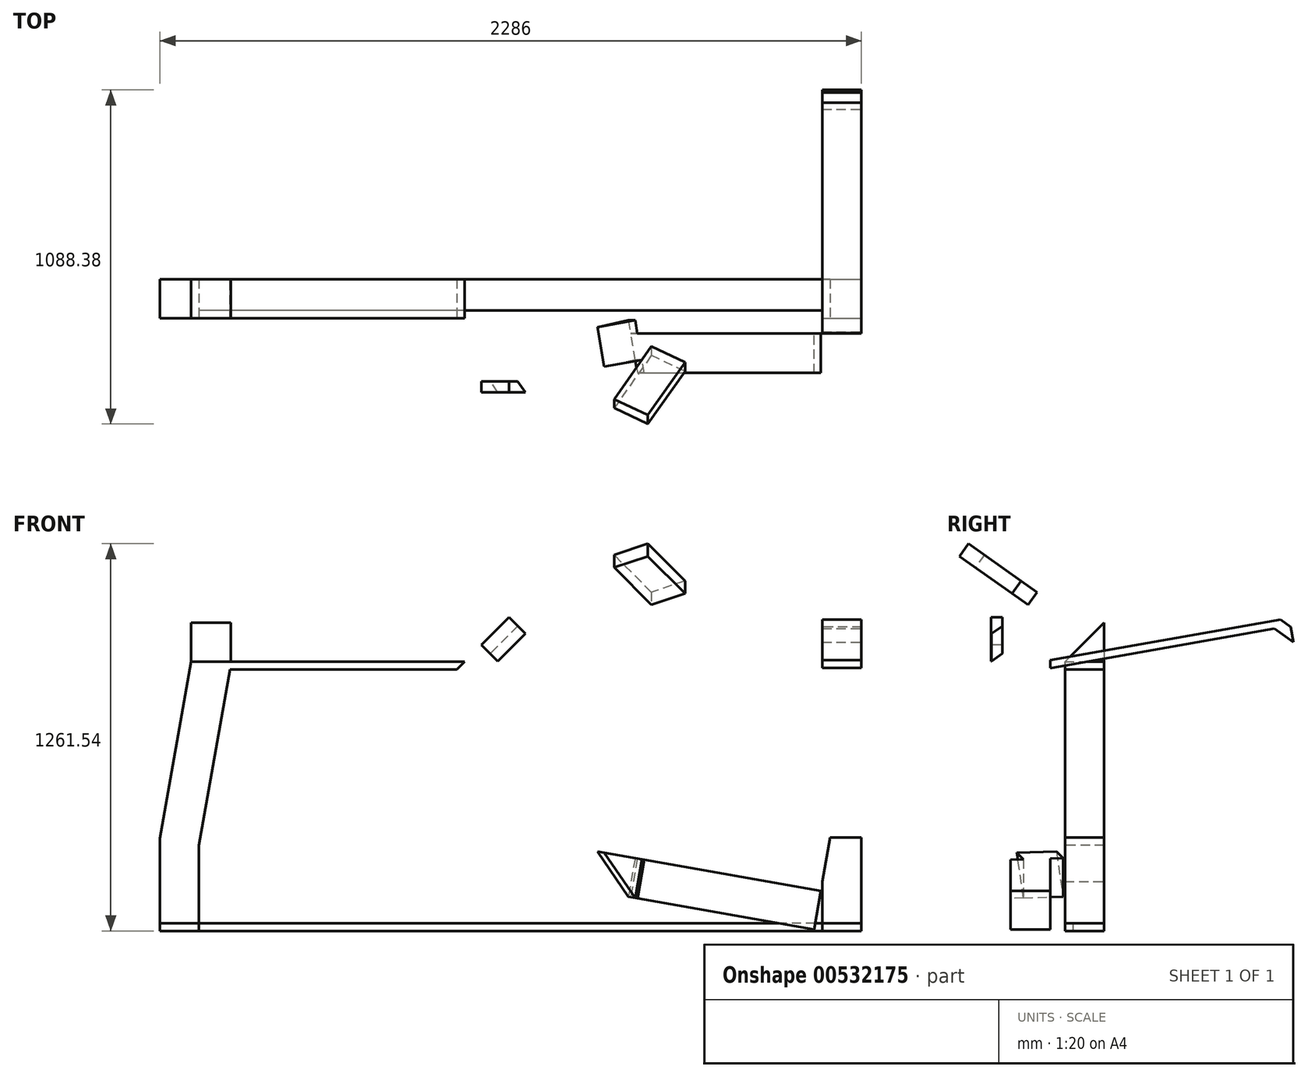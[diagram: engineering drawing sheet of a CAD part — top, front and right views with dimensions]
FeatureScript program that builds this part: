
annotation { "Feature Type Name" : "Feature", "Feature Type Description" : "" }
export const myFeature = defineFeature(function(context is Context, id is Id, definition is map)
    precondition{}
    {
        {
            var Q0;
            Q0=qCreatedBy(makeId("Top.planeOp"),FACE);
            var sketch = newSketch(context, id + "F0", { "sketchPlane" : qUnion([Q0])});
            skLineSegment(sketch, "E0.bottom", {"start": v(0, 0) * mm, "end": v(127, 0) * mm});
            skLineSegment(sketch, "E0.top", {"start": v(0, 127) * mm, "end": v(127, 127) * mm});
            skLineSegment(sketch, "E0.left", {"start": v(0, 0) * mm, "end": v(0, 127) * mm});
            skLineSegment(sketch, "E0.right", {"start": v(127, 0) * mm, "end": v(127, 127) * mm});
            skLineSegment(sketch, "E1.bottom", {"start": v(-2032, 127) * mm, "end": v(-2159, 127) * mm});
            skLineSegment(sketch, "E1.top", {"start": v(-2032, 0) * mm, "end": v(-2159, 0) * mm});
            skLineSegment(sketch, "E1.left", {"start": v(-2032, 127) * mm, "end": v(-2032, 0) * mm});
            skLineSegment(sketch, "E1.right", {"start": v(-2159, 127) * mm, "end": v(-2159, 0) * mm});
            skLineSegment(sketch, "E2.bottom", {"start": v(0, 127) * mm, "end": v(-2032, 127) * mm});
            skLineSegment(sketch, "E2.top", {"start": v(0, 25.4) * mm, "end": v(-2032, 25.4) * mm});
            skLineSegment(sketch, "E2.left", {"start": v(0, 127) * mm, "end": v(0, 25.4) * mm});
            skLineSegment(sketch, "E2.right", {"start": v(-2032, 127) * mm, "end": v(-2032, 25.4) * mm});
            skSolve(sketch);
        }
        {
            var Q0;
            Q0=makeQuery(id+"F0.imprint","IMPRINT",FACE,{"disambiguationData":[TD([[makeQuery(id+"F0.imprint","IMPRINT",EDGE,{"derivedFrom":sQuery(id+"F0.wireOp",EDGE,"E1.bottom")}),1.0]])]});
            var Q1;
            Q1=makeQuery(id+"F0.imprint","IMPRINT",FACE,{"disambiguationData":[TD([[makeQuery(id+"F0.imprint","IMPRINT",EDGE,{"derivedFrom":sQuery(id+"F0.wireOp",EDGE,"E0.bottom")}),1.0]])]});
            extrude(context, id + "F1", {"entities" : qUnion([Q0, Q1]), "depth" : 304.8 * mm, "offsetDistance" : 25.4 * mm});
        }
        {
            var Q0;
            Q0=makeQuery(id+"F1.opExtrude","CAP_EDGE",EDGE,{"disambiguationData":[OSD([sQuery(id+"F0.wireOp",EDGE,"E1.left"),sQuery(id+"F0.wireOp",EDGE,"E2.right")])],"isStart":false});
            chamfer(context, id + "F2", {"entities" : qUnion([Q0]), "chamferType" : ChamferType.OFFSET_ANGLE, "width" : 25.4 * mm, "oppositeDirection" : false, "angle" : 80 * degree, "tangentPropagation" : true});
        }
        {
            var Q0;
            Q0=makeQuery(id+"F1.opExtrude","CAP_EDGE",EDGE,{"disambiguationData":[OSD([sQuery(id+"F0.wireOp",EDGE,"E0.left"),sQuery(id+"F0.wireOp",EDGE,"E2.left")])],"isStart":false});
            chamfer(context, id + "F3", {"entities" : qUnion([Q0]), "chamferType" : ChamferType.OFFSET_ANGLE, "width" : 25.4 * mm, "oppositeDirection" : true, "angle" : 80 * degree, "tangentPropagation" : true});
        }
        {
            var Q0;
            Q0 = qSketchRegion(id + "F0", true);
            extrude(context, id + "F4", {"entities" : qUnion([Q0]), "depth" : 25.4 * mm, "offsetDistance" : 25.4 * mm});
        }
        {
            var Q0;
            Q0=makeQuery(id+"F2.opChamfer","BLEND_FACE",FACE,{"disambiguationData":[OSD([sQuery(id+"F0.wireOp",EDGE,"E1.left"),sQuery(id+"F0.wireOp",EDGE,"E2.right")])]});
            var sketch = newSketch(context, id + "F5", { "sketchPlane" : qUnion([Q0])});
            skLineSegment(sketch, "E3.bottom", {"start": v(-2178.6, 127) * mm, "end": v(-2049.65, 127) * mm});
            skLineSegment(sketch, "E3.top", {"start": v(-2178.6, 0) * mm, "end": v(-2049.65, 0) * mm});
            skLineSegment(sketch, "E3.left", {"start": v(-2178.6, 127) * mm, "end": v(-2178.6, 0) * mm});
            skLineSegment(sketch, "E3.right", {"start": v(-2049.65, 127) * mm, "end": v(-2049.65, 0) * mm});
            skSolve(sketch);
        }
        {
            var Q0;
            Q0 = qSketchRegion(id + "F5", true);
            extrude(context, id + "F6", {"entities" : qUnion([Q0]), "operationType" : NewBodyOperationType.ADD, "depth" : 609.6 * mm, "offsetDistance" : 25.4 * mm});
        }
        {
            var Q0;
            Q0=makeQuery(id+"F3.opChamfer","BLEND_FACE",FACE,{"disambiguationData":[OSD([sQuery(id+"F0.wireOp",EDGE,"E0.left"),sQuery(id+"F0.wireOp",EDGE,"E2.left")])]});
            var sketch = newSketch(context, id + "F7", { "sketchPlane" : qUnion([Q0])});
            skLineSegment(sketch, "E4.bottom", {"start": v(177.48, 127) * mm, "end": v(48.52, 127) * mm});
            skLineSegment(sketch, "E4.top", {"start": v(177.48, 0) * mm, "end": v(48.52, 0) * mm});
            skLineSegment(sketch, "E4.left", {"start": v(177.48, 127) * mm, "end": v(177.48, 0) * mm});
            skLineSegment(sketch, "E4.right", {"start": v(48.52, 127) * mm, "end": v(48.52, 0) * mm});
            skSolve(sketch);
        }
        {
            var Q0;
            Q0 = qSketchRegion(id + "F7", true);
            extrude(context, id + "F8", {"entities" : qUnion([Q0]), "operationType" : NewBodyOperationType.ADD, "depth" : 609.6 * mm, "offsetDistance" : 25.4 * mm});
        }
        {
            var Q0;
            Q0=makeQuery(id+"F8.opExtrude","CAP_EDGE",EDGE,{"disambiguationData":[OSD([sQuery(id+"F7.wireOp",EDGE,"E4.left")])],"isStart":false});
            chamfer(context, id + "F9", {"entities" : qUnion([Q0]), "chamferType" : ChamferType.OFFSET_ANGLE, "width" : 25.4 * mm, "oppositeDirection" : false, "angle" : 80 * degree, "tangentPropagation" : true});
        }
        {
            var Q0;
            Q0=makeQuery(id+"F6.opExtrude","CAP_EDGE",EDGE,{"disambiguationData":[OSD([sQuery(id+"F5.wireOp",EDGE,"E3.left")])],"isStart":false});
            chamfer(context, id + "F10", {"entities" : qUnion([Q0]), "chamferType" : ChamferType.OFFSET_ANGLE, "width" : 25.4 * mm, "oppositeDirection" : false, "angle" : 80 * degree, "tangentPropagation" : true});
        }
        {
            var Q0;
            Q0=makeQuery(id+"F10.opChamfer","BLEND_FACE",FACE,{"disambiguationData":[OSD([sQuery(id+"F5.wireOp",EDGE,"E3.left")])]});
            var sketch = newSketch(context, id + "F11", { "sketchPlane" : qUnion([Q0])});
            skLineSegment(sketch, "E5.bottom", {"start": v(-2057.55, 127) * mm, "end": v(-1926.6, 127) * mm});
            skLineSegment(sketch, "E5.top", {"start": v(-2057.55, 0) * mm, "end": v(-1926.6, 0) * mm});
            skLineSegment(sketch, "E5.left", {"start": v(-2057.55, 127) * mm, "end": v(-2057.55, 0) * mm});
            skLineSegment(sketch, "E5.right", {"start": v(-1926.6, 127) * mm, "end": v(-1926.6, 0) * mm});
            skSolve(sketch);
        }
        {
            var Q0;
            Q0 = qSketchRegion(id + "F11", true);
            extrude(context, id + "F12", {"entities" : qUnion([Q0]), "operationType" : NewBodyOperationType.ADD, "depth" : 127 * mm, "offsetDistance" : 25.4 * mm});
        }
        {
            var Q0;
            Q0=makeQuery(id+"F12.opExtrude","CAP_EDGE",EDGE,{"disambiguationData":[OSD([sQuery(id+"F11.wireOp",EDGE,"E5.top")])],"isStart":false});
            chamfer(context, id + "F13", {"entities" : qUnion([Q0]), "chamferType" : ChamferType.OFFSET_ANGLE, "width" : 127 * mm, "oppositeDirection" : false, "angle" : 45 * degree, "tangentPropagation" : true});
        }
        {
            var Q0;
            Q0=makeQuery(id+"F9.opChamfer","BLEND_FACE",FACE,{"disambiguationData":[OSD([sQuery(id+"F7.wireOp",EDGE,"E4.left")])]});
            var sketch = newSketch(context, id + "F14", { "sketchPlane" : qUnion([Q0])});
            skLineSegment(sketch, "E6.bottom", {"start": v(-105.4, 127) * mm, "end": v(25.55, 127) * mm});
            skLineSegment(sketch, "E6.top", {"start": v(-105.4, 0) * mm, "end": v(25.55, 0) * mm});
            skLineSegment(sketch, "E6.left", {"start": v(-105.4, 127) * mm, "end": v(-105.4, 0) * mm});
            skLineSegment(sketch, "E6.right", {"start": v(25.55, 127) * mm, "end": v(25.55, 0) * mm});
            skSolve(sketch);
        }
        {
            var Q0;
            Q0 = qSketchRegion(id + "F14", true);
            extrude(context, id + "F15", {"entities" : qUnion([Q0]), "operationType" : NewBodyOperationType.ADD, "depth" : 127 * mm, "offsetDistance" : 25.4 * mm});
        }
        {
            var Q0;
            Q0=makeQuery(id+"F15.opExtrude","CAP_EDGE",EDGE,{"disambiguationData":[OSD([sQuery(id+"F14.wireOp",EDGE,"E6.top")])],"isStart":false});
            chamfer(context, id + "F16", {"entities" : qUnion([Q0]), "chamferType" : ChamferType.OFFSET_ANGLE, "width" : 127 * mm, "oppositeDirection" : false, "angle" : 45 * degree, "tangentPropagation" : true});
        }
        {
            var Q0;
            Q0=makeQuery(id+"F6.opExtrude","SWEPT_FACE",FACE,{"disambiguationData":[OSD([sQuery(id+"F5.wireOp",EDGE,"E3.right")])]});
            var sketch = newSketch(context, id + "F17", { "sketchPlane" : qUnion([Q0])});
            skLineSegment(sketch, "E7.bottom", {"start": v(0, 529.24) * mm, "end": v(127, 529.24) * mm});
            skLineSegment(sketch, "E7.top", {"start": v(0, 503.84) * mm, "end": v(127, 503.84) * mm});
            skLineSegment(sketch, "E7.left", {"start": v(0, 529.24) * mm, "end": v(0, 503.84) * mm});
            skLineSegment(sketch, "E7.right", {"start": v(127, 529.24) * mm, "end": v(127, 503.84) * mm});
            skSolve(sketch);
        }
        {
            var Q0;
            Q0 = qSketchRegion(id + "F17", true);
            extrude(context, id + "F18", {"entities" : qUnion([Q0]), "operationType" : NewBodyOperationType.ADD, "depth" : 2.54 * mm, "offsetDistance" : 25.4 * mm});
        }
        {
            var Q0;
            Q0=makeQuery(id+"F18.opExtrude","CAP_EDGE",EDGE,{"disambiguationData":[OSD([sQuery(id+"F17.wireOp",EDGE,"E7.bottom")])],"isStart":false});
            chamfer(context, id + "F19", {"entities" : qUnion([Q0]), "chamferType" : ChamferType.OFFSET_ANGLE, "width" : 25.4 * mm, "oppositeDirection" : false, "angle" : 10 * degree, "tangentPropagation" : true});
        }
        {
            var Q0;
            Q0=makeQuery(id+"F19.opChamfer","BLEND_FACE",FACE,{"disambiguationData":[OSD([sQuery(id+"F17.wireOp",EDGE,"E7.bottom")])]});
            var sketch = newSketch(context, id + "F20", { "sketchPlane" : qUnion([Q0])});
            skLineSegment(sketch, "E8.bottom", {"start": v(0, 877.12) * mm, "end": v(127, 877.12) * mm});
            skLineSegment(sketch, "E8.top", {"start": v(0, 851.66) * mm, "end": v(127, 851.66) * mm});
            skLineSegment(sketch, "E8.left", {"start": v(0, 877.12) * mm, "end": v(0, 851.66) * mm});
            skLineSegment(sketch, "E8.right", {"start": v(127, 877.12) * mm, "end": v(127, 851.66) * mm});
            skSolve(sketch);
        }
        {
            var Q0;
            Q0 = qSketchRegion(id + "F20", true);
            extrude(context, id + "F21", {"entities" : qUnion([Q0]), "operationType" : NewBodyOperationType.ADD, "depth" : 762 * mm, "offsetDistance" : 25.4 * mm});
        }
        {
            var Q0;
            Q0=makeQuery(id+"F8.opExtrude","SWEPT_FACE",FACE,{"disambiguationData":[OSD([sQuery(id+"F7.wireOp",EDGE,"E4.right")])]});
            var sketch = newSketch(context, id + "F22", { "sketchPlane" : qUnion([Q0])});
            skLineSegment(sketch, "E9.bottom", {"start": v(0, 882.1) * mm, "end": v(-127, 882.1) * mm});
            skLineSegment(sketch, "E9.top", {"start": v(0, 856.7) * mm, "end": v(-127, 856.7) * mm});
            skLineSegment(sketch, "E9.left", {"start": v(0, 882.1) * mm, "end": v(0, 856.7) * mm});
            skLineSegment(sketch, "E9.right", {"start": v(-127, 882.1) * mm, "end": v(-127, 856.7) * mm});
            skSolve(sketch);
        }
        {
            var Q0;
            Q0 = qSketchRegion(id + "F22", true);
            extrude(context, id + "F23", {"entities" : qUnion([Q0]), "operationType" : NewBodyOperationType.ADD, "depth" : 5.08 * mm, "offsetDistance" : 25.4 * mm});
        }
        {
            var Q0;
            Q0=makeQuery(id+"F23.opExtrude","CAP_EDGE",EDGE,{"disambiguationData":[OSD([sQuery(id+"F22.wireOp",EDGE,"E9.bottom")])],"isStart":false});
            chamfer(context, id + "F24", {"entities" : qUnion([Q0]), "chamferType" : ChamferType.OFFSET_ANGLE, "width" : 25.4 * mm, "oppositeDirection" : false, "angle" : 10 * degree, "tangentPropagation" : true});
        }
        {
            var Q0;
            Q0=makeQuery(id+"F24.opChamfer","BLEND_FACE",FACE,{"disambiguationData":[OSD([sQuery(id+"F22.wireOp",EDGE,"E9.bottom")])]});
            var sketch = newSketch(context, id + "F25", { "sketchPlane" : qUnion([Q0])});
            skLineSegment(sketch, "E10.bottom", {"start": v(-127, 877.01) * mm, "end": v(0, 877.01) * mm});
            skLineSegment(sketch, "E10.top", {"start": v(-127, 851.22) * mm, "end": v(0, 851.22) * mm});
            skLineSegment(sketch, "E10.left", {"start": v(-127, 877.01) * mm, "end": v(-127, 851.22) * mm});
            skLineSegment(sketch, "E10.right", {"start": v(0, 877.01) * mm, "end": v(0, 851.22) * mm});
            skSolve(sketch);
        }
        {
            var Q0;
            Q0 = qSketchRegion(id + "F25", true);
            extrude(context, id + "F26", {"entities" : qUnion([Q0]), "operationType" : NewBodyOperationType.ADD, "depth" : 762 * mm, "offsetDistance" : 25.4 * mm});
        }
        {
            var Q0;
            Q0=makeQuery(id+"F26.opExtrude","CAP_EDGE",EDGE,{"disambiguationData":[OSD([sQuery(id+"F25.wireOp",EDGE,"E10.top")])],"isStart":false});
            chamfer(context, id + "F27", {"entities" : qUnion([Q0]), "chamferType" : ChamferType.OFFSET_ANGLE, "width" : 25.4 * mm, "oppositeDirection" : false, "angle" : 45 * degree, "tangentPropagation" : true});
        }
        {
            var Q0;
            Q0=makeQuery(id+"F27.opChamfer","BLEND_FACE",FACE,{"disambiguationData":[OSD([sQuery(id+"F25.wireOp",EDGE,"E10.top")])]});
            var sketch = newSketch(context, id + "F28", { "sketchPlane" : qUnion([Q0])});
            skLineSegment(sketch, "E11.bottom", {"start": v(-127, 1233.62) * mm, "end": v(0, 1233.62) * mm});
            skLineSegment(sketch, "E11.top", {"start": v(-127, 1197.7) * mm, "end": v(0, 1197.7) * mm});
            skLineSegment(sketch, "E11.left", {"start": v(-127, 1233.62) * mm, "end": v(-127, 1197.7) * mm});
            skLineSegment(sketch, "E11.right", {"start": v(0, 1233.62) * mm, "end": v(0, 1197.7) * mm});
            skSolve(sketch);
        }
        {
            var Q0;
            Q0 = qSketchRegion(id + "F28", true);
            extrude(context, id + "F29", {"entities" : qUnion([Q0]), "operationType" : NewBodyOperationType.ADD, "depth" : 76.2 * mm, "offsetDistance" : 25.4 * mm});
        }
        {
            var Q0;
            Q0=makeQuery(id+"F21.opExtrude","CAP_EDGE",EDGE,{"disambiguationData":[OSD([sQuery(id+"F20.wireOp",EDGE,"E8.top")])],"isStart":false});
            chamfer(context, id + "F30", {"entities" : qUnion([Q0]), "chamferType" : ChamferType.OFFSET_ANGLE, "width" : 25.4 * mm, "oppositeDirection" : false, "angle" : 45 * degree, "tangentPropagation" : true});
        }
        {
            var Q0;
            Q0=makeQuery(id+"F30.opChamfer","BLEND_FACE",FACE,{"disambiguationData":[OSD([sQuery(id+"F20.wireOp",EDGE,"E8.top")])]});
            var sketch = newSketch(context, id + "F31", { "sketchPlane" : qUnion([Q0])});
            skLineSegment(sketch, "E12.bottom", {"start": v(-204.67, 0) * mm, "end": v(-240.6, 0) * mm});
            skLineSegment(sketch, "E12.top", {"start": v(-204.67, -127) * mm, "end": v(-240.6, -127) * mm});
            skLineSegment(sketch, "E12.left", {"start": v(-204.67, 0) * mm, "end": v(-204.67, -127) * mm});
            skLineSegment(sketch, "E12.right", {"start": v(-240.6, 0) * mm, "end": v(-240.6, -127) * mm});
            skSolve(sketch);
        }
        {
            var Q0;
            Q0 = qSketchRegion(id + "F31", true);
            extrude(context, id + "F32", {"entities" : qUnion([Q0]), "operationType" : NewBodyOperationType.ADD, "depth" : 76.2 * mm, "offsetDistance" : 25.4 * mm});
        }
        {
            var Q0;
            Q0=makeQuery(id+"F32.opExtrude","CAP_EDGE",EDGE,{"disambiguationData":[OSD([sQuery(id+"F31.wireOp",EDGE,"E12.left")])],"isStart":false});
            chamfer(context, id + "F33", {"entities" : qUnion([Q0]), "chamferType" : ChamferType.OFFSET_ANGLE, "width" : 35.56 * mm, "oppositeDirection" : false, "angle" : 45 * degree, "tangentPropagation" : true});
        }
        {
            var Q0;
            Q0=makeQuery(id+"F29.opExtrude","CAP_EDGE",EDGE,{"disambiguationData":[OSD([sQuery(id+"F28.wireOp",EDGE,"E11.bottom")])],"isStart":false});
            chamfer(context, id + "F34", {"entities" : qUnion([Q0]), "chamferType" : ChamferType.OFFSET_ANGLE, "width" : 35.56 * mm, "oppositeDirection" : false, "angle" : 45 * degree, "tangentPropagation" : true});
        }
        {
            var Q0;
            Q0=makeQuery(id+"F33.opChamfer","BLEND_FACE",FACE,{"disambiguationData":[OSD([sQuery(id+"F31.wireOp",EDGE,"E12.left")])]});
            var sketch = newSketch(context, id + "F35", { "sketchPlane" : qUnion([Q0])});
            skLineSegment(sketch, "E13.bottom", {"start": v(0, 848.33) * mm, "end": v(127, 848.33) * mm});
            skLineSegment(sketch, "E13.top", {"start": v(0, 798.04) * mm, "end": v(127, 798.04) * mm});
            skLineSegment(sketch, "E13.left", {"start": v(0, 848.33) * mm, "end": v(0, 798.04) * mm});
            skLineSegment(sketch, "E13.right", {"start": v(127, 848.33) * mm, "end": v(127, 798.04) * mm});
            skSolve(sketch);
        }
        {
            var Q0;
            Q0 = qSketchRegion(id + "F35", true);
            extrude(context, id + "F36", {"entities" : qUnion([Q0]), "operationType" : NewBodyOperationType.ADD, "depth" : 242.57 * mm, "offsetDistance" : 25.4 * mm});
        }
    });
